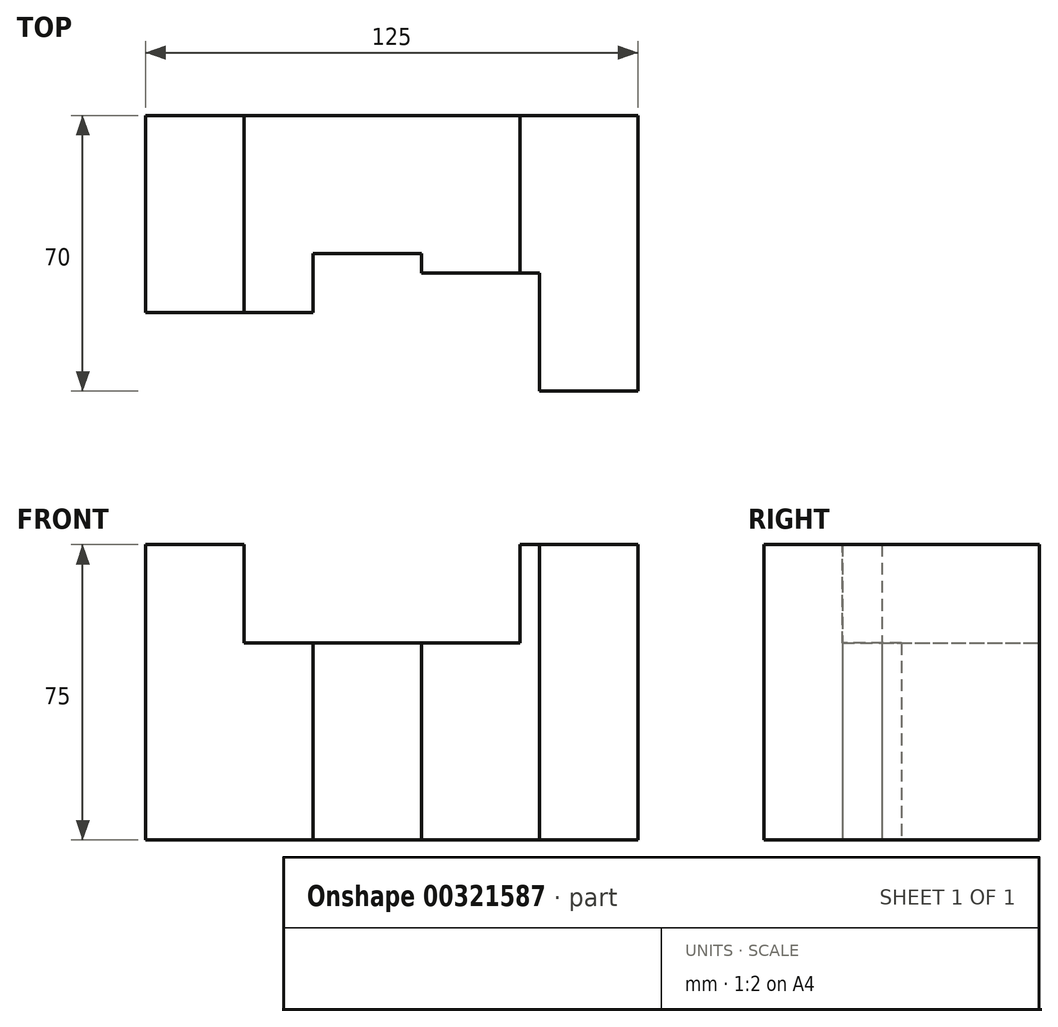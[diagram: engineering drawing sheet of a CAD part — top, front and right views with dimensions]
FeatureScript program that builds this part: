
annotation { "Feature Type Name" : "Feature", "Feature Type Description" : "" }
export const myFeature = defineFeature(function(context is Context, id is Id, definition is map)
    precondition{}
    {
        {
            var Q0;
            Q0=qCreatedBy(makeId("Front.planeOp"),FACE);
            var sketch = newSketch(context, id + "F0", { "sketchPlane" : qUnion([Q0])});
            skLineSegment(sketch, "E0", {"start": v(0, 0) * mm, "end": v(0, 75) * mm});
            skLineSegment(sketch, "E1", {"start": v(0, 75) * mm, "end": v(25, 75) * mm});
            skLineSegment(sketch, "E2", {"start": v(25, 75) * mm, "end": v(25, 50) * mm});
            skLineSegment(sketch, "E3", {"start": v(25, 50) * mm, "end": v(95, 50) * mm});
            skLineSegment(sketch, "E4", {"start": v(95, 50) * mm, "end": v(95, 75) * mm});
            skLineSegment(sketch, "E5", {"start": v(95, 75) * mm, "end": v(125, 75) * mm});
            skLineSegment(sketch, "E6", {"start": v(125, 75) * mm, "end": v(125, 0) * mm});
            skLineSegment(sketch, "E7", {"start": v(125, 0) * mm, "end": v(0, 0) * mm});
            skSolve(sketch);
        }
        {
            var Q0;
            Q0 = qSketchRegion(id + "F0", true);
            extrude(context, id + "F1", {"entities" : qUnion([Q0]), "depth" : 70 * mm});
        }
        {
            var Q0;
            Q0=qCreatedBy(makeId("Top.planeOp"),FACE);
            var sketch = newSketch(context, id + "F2", { "sketchPlane" : qUnion([Q0])});
            skLineSegment(sketch, "E8", {"start": v(100, -70) * mm, "end": v(0, -70) * mm});
            skLineSegment(sketch, "E9", {"start": v(0, -70) * mm, "end": v(0, -50) * mm});
            skLineSegment(sketch, "E10", {"start": v(0, -50) * mm, "end": v(42.5, -50) * mm});
            skLineSegment(sketch, "E11", {"start": v(42.5, -50) * mm, "end": v(42.5, -35) * mm});
            skLineSegment(sketch, "E12", {"start": v(42.5, -35) * mm, "end": v(70, -35) * mm});
            skLineSegment(sketch, "E13", {"start": v(70, -35) * mm, "end": v(70, -40) * mm});
            skLineSegment(sketch, "E14", {"start": v(70, -40) * mm, "end": v(100, -40) * mm});
            skLineSegment(sketch, "E15", {"start": v(100, -40) * mm, "end": v(100, -70) * mm});
            skSolve(sketch);
        }
        {
            var Q0;
            Q0 = qSketchRegion(id + "F2", true);
            extrude(context, id + "F3", {"entities" : qUnion([Q0]), "operationType" : NewBodyOperationType.REMOVE, "endBound" : BoundingType.THROUGH_ALL, "depth" : 25 * mm});
        }
    });
